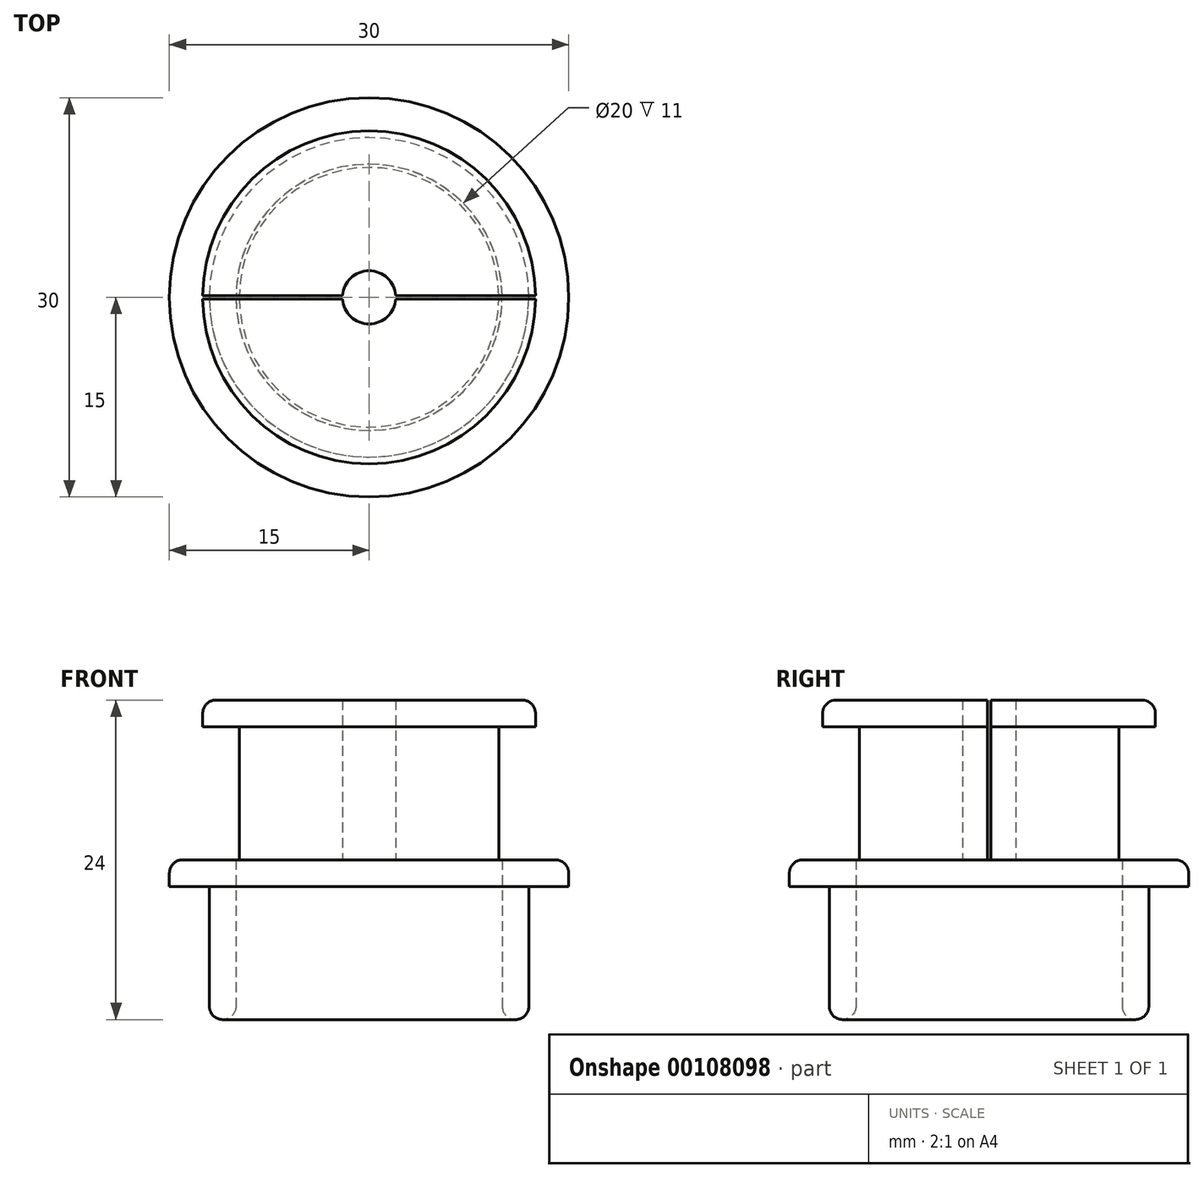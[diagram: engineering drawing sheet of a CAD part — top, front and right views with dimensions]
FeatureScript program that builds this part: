
annotation { "Feature Type Name" : "Feature", "Feature Type Description" : "" }
export const myFeature = defineFeature(function(context is Context, id is Id, definition is map)
    precondition{}
    {
        {
            var Q0;
            Q0=qCreatedBy(makeId("Front.planeOp"),FACE);
            var sketch = newSketch(context, id + "F0", { "sketchPlane" : qUnion([Q0])});
            skLineSegment(sketch, "E0", {"start": v(10, 0) * mm, "end": v(10, 12) * mm});
            skLineSegment(sketch, "E1", {"start": v(10, 12) * mm, "end": v(15, 12) * mm});
            skLineSegment(sketch, "E2", {"start": v(15, 12) * mm, "end": v(15, 10) * mm});
            skLineSegment(sketch, "E3", {"start": v(15, 10) * mm, "end": v(12, 10) * mm});
            skLineSegment(sketch, "E4", {"start": v(12, 10) * mm, "end": v(12, 0) * mm});
            skLineSegment(sketch, "E5", {"start": v(12, 0) * mm, "end": v(10, 0) * mm});
            skLineSegment(sketch, "E6", {"start": v(0, 0) * mm, "end": v(0, 28.43) * mm, "construction": true});
            skSolve(sketch);
        }
        {
            var Q0;
            Q0 = qSketchRegion(id + "F0", true);
            var Q1;
            Q1=sQuery(id+"F0.wireOp",EDGE,"E6");
            revolve(context, id + "F1", {"entities" : qUnion([Q0]), "axis" : qUnion([Q1]), "revolveType" : RevolveType.FULL});
        }
        {
            var Q0;
            Q0=makeQuery(id+"F1.opRevolve","SWEPT_FACE",FACE,{"disambiguationData":[OSD([sQuery(id+"F0.wireOp",EDGE,"E5")])]});
            var Q1;
            Q1=makeQuery(id+"F1.opRevolve","SWEPT_EDGE",EDGE,{"disambiguationData":[OSD([sQuery(id+"F0.wireOp",EDGE,"E1"),sQuery(id+"F0.wireOp",EDGE,"E2")])]});
            fillet(context, id + "F2", {"entities" : qUnion([Q0, Q1]), "radius" : 1 * mm, "tangentPropagation" : true, "allowEdgeOverflow" : false});
        }
        {
            var Q0;
            Q0=makeQuery(id+"F1.opRevolve","SWEPT_FACE",FACE,{"disambiguationData":[OSD([sQuery(id+"F0.wireOp",EDGE,"E1")])]});
            var sketch = newSketch(context, id + "F3", { "sketchPlane" : qUnion([Q0])});
            skCircle(sketch, "E7", {"center": v(0, 0) * mm, "radius": 2 * mm});
            skCircle(sketch, "E8.0", {"center": v(0, 0) * mm, "radius": 9.75 * mm});
            skSolve(sketch);
        }
        {
            var Q0;
            Q0 = qSketchRegion(id + "F3", true);
            extrude(context, id + "F4", {"entities" : qUnion([Q0]), "depth" : 10 * mm});
        }
        {
            var Q0;
            Q0=makeQuery(id+"F4.opExtrude","CAP_FACE",FACE,{"disambiguationData":[OSD([sQuery(id+"F3.wireOp",EDGE,"IUFRcDTU-90hC-QJ4P-FrYf-4yOveknkrDAy"),sQuery(id+"F3.wireOp",EDGE,"E7")])],"isStart":false});
            var sketch = newSketch(context, id + "F5", { "sketchPlane" : qUnion([Q0])});
            skCircle(sketch, "E9.0", {"center": v(0, 0) * mm, "radius": 2 * mm});
            skCircle(sketch, "E10", {"center": v(0, 0) * mm, "radius": 12.5 * mm});
            skSolve(sketch);
        }
        {
            var Q0;
            Q0 = qSketchRegion(id + "F5", true);
            extrude(context, id + "F6", {"entities" : qUnion([Q0]), "operationType" : NewBodyOperationType.ADD, "depth" : 2 * mm});
        }
        {
            var Q0;
            Q0=makeQuery(id+"F6.opExtrude","CAP_EDGE",EDGE,{"disambiguationData":[OSD([sQuery(id+"F5.wireOp",EDGE,"E10")])],"isStart":false});
            var Q1;
            Q1=makeQuery(id+"F4.opExtrude","CAP_EDGE",EDGE,{"disambiguationData":[OSD([sQuery(id+"F3.wireOp",EDGE,"IUFRcDTU-90hC-QJ4P-FrYf-4yOveknkrDAy")])],"isStart":true});
            fillet(context, id + "F7", {"entities" : qUnion([Q0, Q1]), "radius" : 1 * mm, "tangentPropagation" : true, "allowEdgeOverflow" : false});
        }
        {
            var Q0;
            Q0=makeQuery(id+"F6.opExtrude","CAP_FACE",FACE,{"disambiguationData":[OSD([sQuery(id+"F5.wireOp",EDGE,"E9.0"),sQuery(id+"F5.wireOp",EDGE,"E10")])],"isStart":false});
            var sketch = newSketch(context, id + "F8", { "sketchPlane" : qUnion([Q0])});
            skLineSegment(sketch, "E11.bottom", {"start": v(12.5, -0.12) * mm, "end": v(-12.5, -0.13) * mm});
            skLineSegment(sketch, "E11.top", {"start": v(12.5, 0.13) * mm, "end": v(-12.5, 0.12) * mm});
            skLineSegment(sketch, "E11.left", {"start": v(12.5, -0.12) * mm, "end": v(12.5, 0.13) * mm});
            skLineSegment(sketch, "E11.right", {"start": v(-12.5, -0.13) * mm, "end": v(-12.5, 0.12) * mm});
            skPoint(sketch, "E11.middle", {"position": v(0, 0) * mm});
            skSolve(sketch);
        }
        {
            var Q0;
            Q0 = qSketchRegion(id + "F8", true);
            var Q1;
            Q1=makeQuery(id+"F4.opExtrude","CAP_FACE",FACE,{"disambiguationData":[OSD([sQuery(id+"F3.wireOp",EDGE,"IUFRcDTU-90hC-QJ4P-FrYf-4yOveknkrDAy"),sQuery(id+"F3.wireOp",EDGE,"E7")])],"isStart":true});
            extrude(context, id + "F9", {"entities" : qUnion([Q0]), "operationType" : NewBodyOperationType.REMOVE, "endBound" : BoundingType.UP_TO_SURFACE, "oppositeDirection" : true, "endBoundEntityFace" : qUnion([Q1]), "depth" : 25 * mm});
        }
    });
